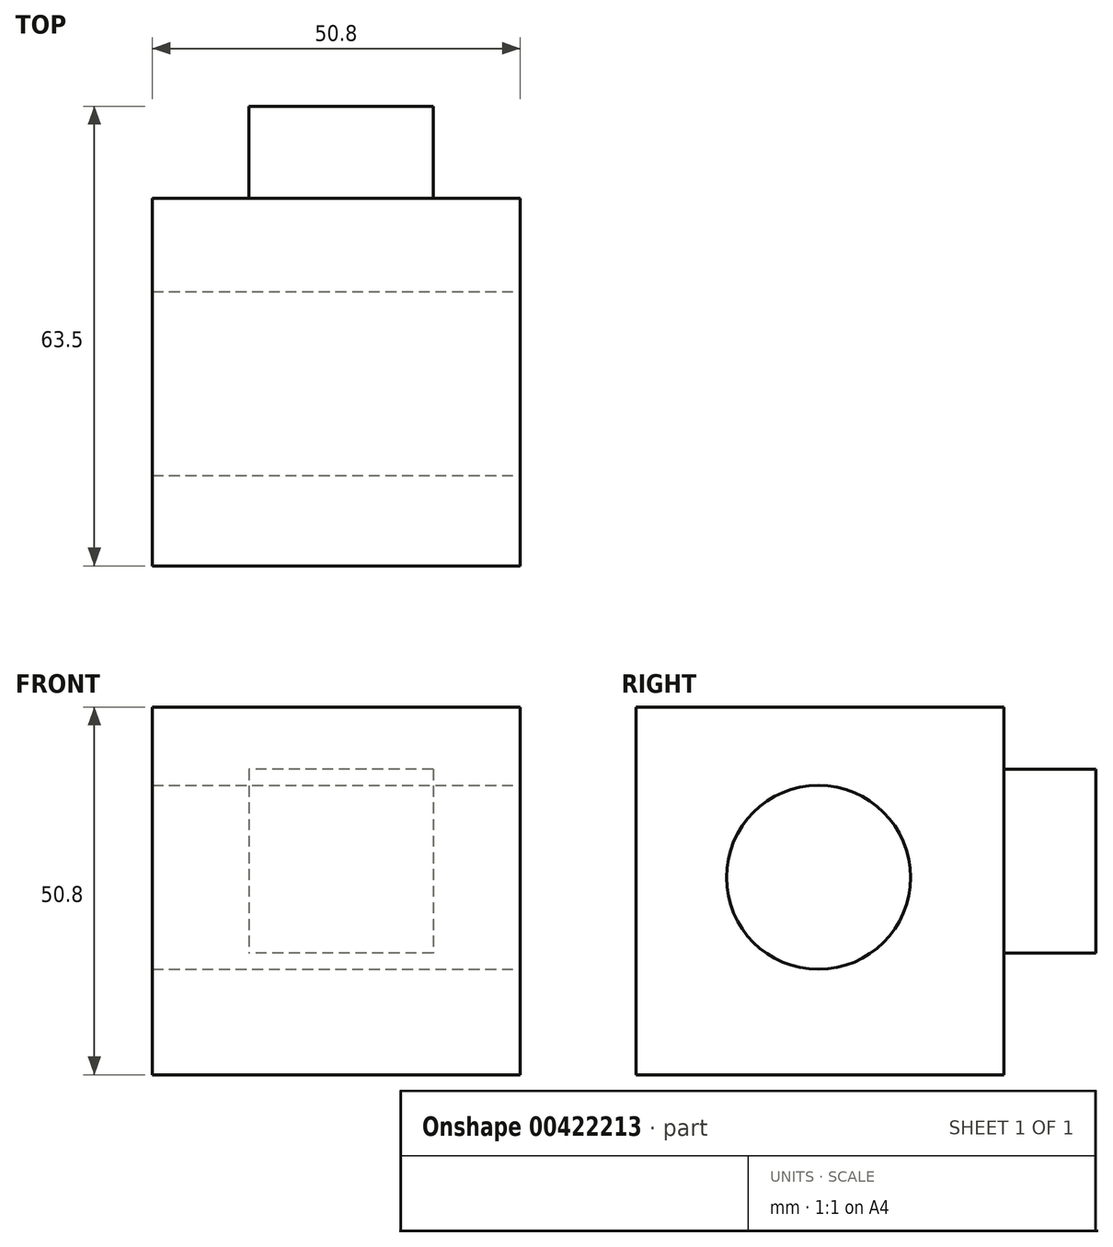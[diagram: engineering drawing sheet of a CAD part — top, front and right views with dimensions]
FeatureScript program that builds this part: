
annotation { "Feature Type Name" : "Feature", "Feature Type Description" : "" }
export const myFeature = defineFeature(function(context is Context, id is Id, definition is map)
    precondition{}
    {
        {
            var Q0;
            Q0=qCreatedBy(makeId("Right.planeOp"),FACE);
            var sketch = newSketch(context, id + "F0", { "sketchPlane" : qUnion([Q0])});
            skLineSegment(sketch, "E0.bottom", {"start": v(-59.2, 58.82) * mm, "end": v(-8.4, 58.82) * mm});
            skLineSegment(sketch, "E0.top", {"start": v(-59.2, 8.02) * mm, "end": v(-8.4, 8.02) * mm});
            skLineSegment(sketch, "E0.left", {"start": v(-59.2, 58.82) * mm, "end": v(-59.2, 8.02) * mm});
            skLineSegment(sketch, "E0.right", {"start": v(-8.4, 58.82) * mm, "end": v(-8.4, 8.02) * mm});
            skSolve(sketch);
        }
        {
            var Q0;
            Q0=makeQuery(id+"F0.imprint","IMPRINT",FACE,{"disambiguationData":[TD([[makeQuery(id+"F0.imprint","IMPRINT",EDGE,{"derivedFrom":sQuery(id+"F0.wireOp",EDGE,"E0.bottom")}),-1.0]])]});
            extrude(context, id + "F1", {"entities" : qUnion([Q0]), "depth" : 50.8 * mm});
        }
        {
            var Q0;
            Q0=makeQuery(id+"F1.opExtrude","CAP_FACE",FACE,{"disambiguationData":[OSD([sQuery(id+"F0.wireOp",EDGE,"E0.bottom"),sQuery(id+"F0.wireOp",EDGE,"E0.top"),sQuery(id+"F0.wireOp",EDGE,"E0.left"),sQuery(id+"F0.wireOp",EDGE,"E0.right")])],"isStart":false});
            var sketch = newSketch(context, id + "F2", { "sketchPlane" : qUnion([Q0])});
            skCircle(sketch, "E1", {"center": v(-34.01, 35.28) * mm, "radius": 12.7 * mm});
            skSolve(sketch);
        }
        {
            var Q0;
            Q0=makeQuery(id+"F2.imprint","IMPRINT",FACE,{"disambiguationData":[TD([[makeQuery(id+"F2.imprint","IMPRINT",EDGE,{"derivedFrom":sQuery(id+"F2.wireOp",EDGE,"E1")}),1.0]])]});
            extrude(context, id + "F3", {"entities" : qUnion([Q0]), "operationType" : NewBodyOperationType.REMOVE, "oppositeDirection" : true, "depth" : 50.8 * mm});
        }
        {
            var Q0;
            Q0=makeQuery(id+"F1.opExtrude","SWEPT_FACE",FACE,{"disambiguationData":[OSD([sQuery(id+"F0.wireOp",EDGE,"E0.right")])]});
            var sketch = newSketch(context, id + "F4", { "sketchPlane" : qUnion([Q0])});
            skLineSegment(sketch, "E2.bottom", {"start": v(-38.77, 50.22) * mm, "end": v(-13.37, 50.22) * mm});
            skLineSegment(sketch, "E2.top", {"start": v(-38.77, 24.82) * mm, "end": v(-13.37, 24.82) * mm});
            skLineSegment(sketch, "E2.left", {"start": v(-38.77, 50.22) * mm, "end": v(-38.77, 24.82) * mm});
            skLineSegment(sketch, "E2.right", {"start": v(-13.37, 50.22) * mm, "end": v(-13.37, 24.82) * mm});
            skSolve(sketch);
        }
        {
            var Q0;
            Q0=makeQuery(id+"F4.imprint","IMPRINT",FACE,{"disambiguationData":[TD([[makeQuery(id+"F4.imprint","IMPRINT",EDGE,{"derivedFrom":sQuery(id+"F4.wireOp",EDGE,"E2.bottom")}),-1.0]])]});
            extrude(context, id + "F5", {"entities" : qUnion([Q0]), "operationType" : NewBodyOperationType.ADD, "depth" : 12.7 * mm});
        }
    });
